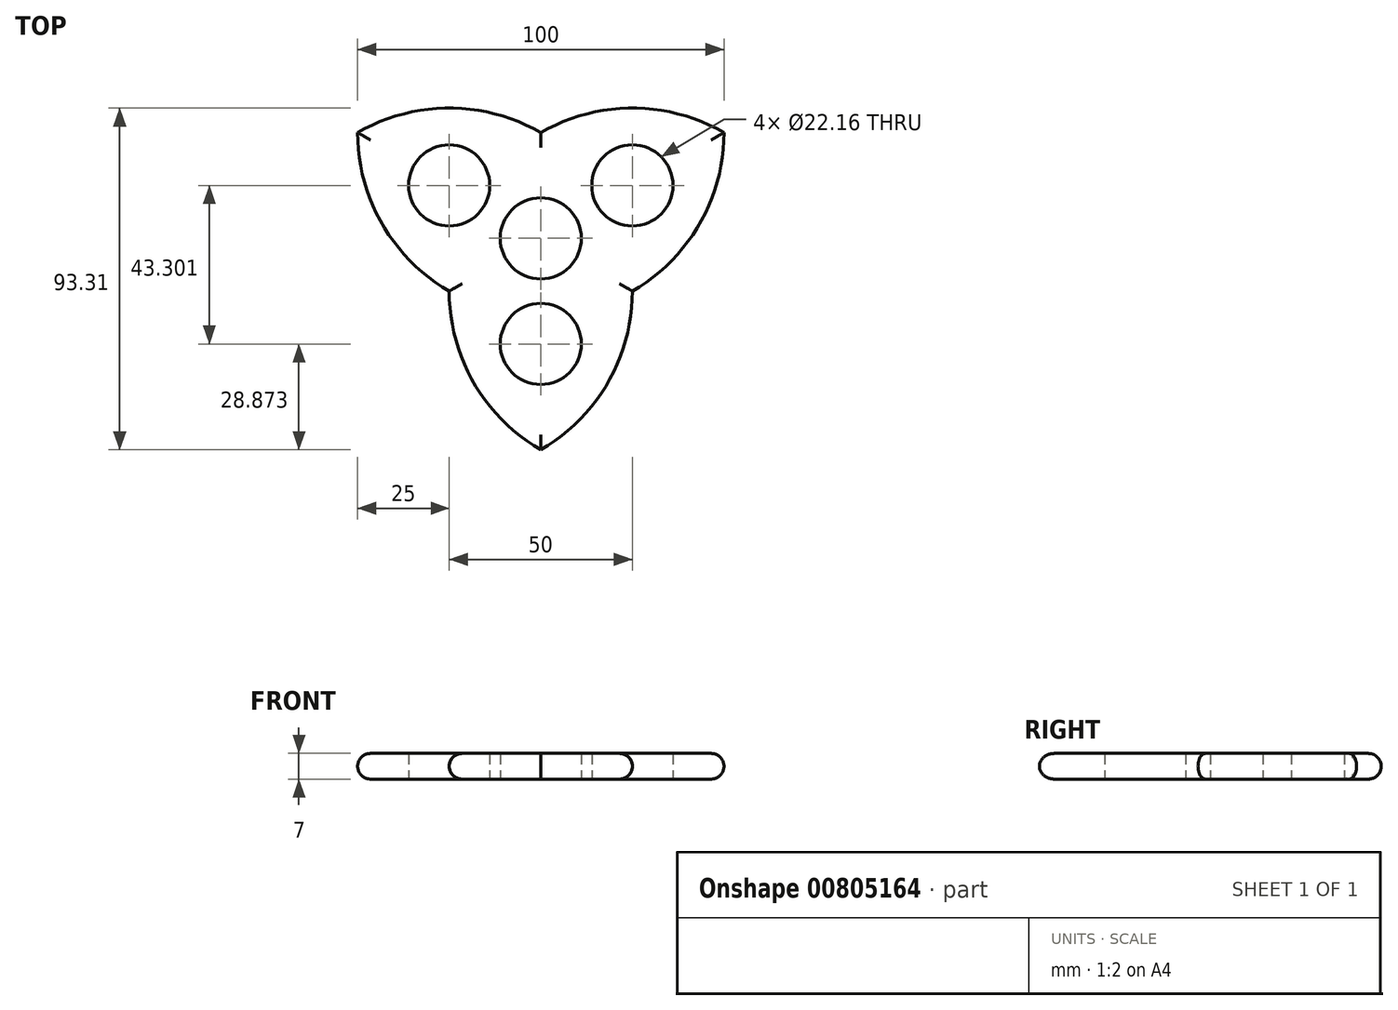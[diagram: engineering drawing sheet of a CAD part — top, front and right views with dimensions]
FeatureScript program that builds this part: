
annotation { "Feature Type Name" : "Feature", "Feature Type Description" : "" }
export const myFeature = defineFeature(function(context is Context, id is Id, definition is map)
    precondition{}
    {
        {
            var Q0;
            Q0=qCreatedBy(makeId("Top.planeOp"),FACE);
            var sketch = newSketch(context, id + "F0", { "sketchPlane" : qUnion([Q0])});
            skCircle(sketch, "E0.cCircle", {"center": v(0, 0) * mm, "radius": 14.43 * mm, "construction": true});
            skLineSegment(sketch, "E0.0", {"start": v(25, -14.43) * mm, "end": v(-25, -14.43) * mm, "construction": true});
            skLineSegment(sketch, "E0.1", {"start": v(-25, -14.43) * mm, "end": v(0, 28.87) * mm, "construction": true});
            skLineSegment(sketch, "E0.2", {"start": v(0, 28.87) * mm, "end": v(25, -14.43) * mm, "construction": true});
            skPoint(sketch, "E0.0.midPoint", {"position": v(0, -14.43) * mm});
            skArc(sketch, "E1", {"start": v(0, -57.74) * mm, "mid": v(18.3, -39.43) * mm, "end": v(25, -14.43) * mm});
            skArc(sketch, "E2", {"start": v(-50, 28.87) * mm, "mid": v(-43.3, 3.87) * mm, "end": v(-25, -14.43) * mm});
            skArc(sketch, "E3", {"start": v(50, 28.87) * mm, "mid": v(25, 35.57) * mm, "end": v(0, 28.87) * mm});
            skCircle(sketch, "E4", {"center": v(0, 0) * mm, "radius": 11.08 * mm});
            skArc(sketch, "E5.trimOffspring", {"start": v(0, 28.87) * mm, "mid": v(-25, 35.57) * mm, "end": v(-50, 28.87) * mm});
            skArc(sketch, "E6.trimOffspring", {"start": v(-25, -14.43) * mm, "mid": v(-18.3, -39.43) * mm, "end": v(0, -57.74) * mm});
            skArc(sketch, "E7.trimOffspring", {"start": v(25, -14.43) * mm, "mid": v(43.3, 3.87) * mm, "end": v(50, 28.87) * mm});
            skLineSegment(sketch, "E8", {"start": v(-25, -14.43) * mm, "end": v(-50, 28.87) * mm, "construction": true});
            skLineSegment(sketch, "E9", {"start": v(0, 28.87) * mm, "end": v(-50, 28.87) * mm, "construction": true});
            skLineSegment(sketch, "E10", {"start": v(-25, 28.87) * mm, "end": v(-25, -14.43) * mm, "construction": true});
            skLineSegment(sketch, "E11", {"start": v(0, 28.87) * mm, "end": v(-37.5, 7.22) * mm, "construction": true});
            skCircle(sketch, "E12", {"center": v(-25, 14.43) * mm, "radius": 11.08 * mm});
            skLineSegment(sketch, "E13.1.0", {"start": v(-25, -14.43) * mm, "end": v(0, -57.74) * mm, "construction": true});
            skLineSegment(sketch, "E13.1.1", {"start": v(25, -14.43) * mm, "end": v(0, -57.74) * mm, "construction": true});
            skCircle(sketch, "E13.1.2", {"center": v(0, -28.87) * mm, "radius": 11.08 * mm});
            skLineSegment(sketch, "E13.1.3", {"start": v(-25, -14.43) * mm, "end": v(12.5, -36.08) * mm, "construction": true});
            skLineSegment(sketch, "E13.1.4", {"start": v(-12.5, -36.08) * mm, "end": v(25, -14.43) * mm, "construction": true});
            skLineSegment(sketch, "E13.2.0", {"start": v(25, -14.43) * mm, "end": v(50, 28.87) * mm, "construction": true});
            skLineSegment(sketch, "E13.2.1", {"start": v(0, 28.87) * mm, "end": v(50, 28.87) * mm, "construction": true});
            skCircle(sketch, "E13.2.2", {"center": v(25, 14.43) * mm, "radius": 11.08 * mm});
            skLineSegment(sketch, "E13.2.3", {"start": v(25, -14.43) * mm, "end": v(25, 28.87) * mm, "construction": true});
            skLineSegment(sketch, "E13.2.4", {"start": v(37.5, 7.22) * mm, "end": v(0, 28.87) * mm, "construction": true});
            skSolve(sketch);
        }
        {
            var Q0;
            Q0=makeQuery(id+"F0.imprint","IMPRINT",FACE,{"disambiguationData":[TD([[makeQuery(id+"F0.imprint","IMPRINT",EDGE,{"derivedFrom":sQuery(id+"F0.wireOp",EDGE,"E1")}),1.0]])]});
            extrude(context, id + "F1", {"entities" : qUnion([Q0]), "depth" : 7 * mm, "offsetDistance" : 25 * mm});
        }
        {
            var Q0;
            Q0=makeQuery(id+"F1.opExtrude","CAP_EDGE",EDGE,{"disambiguationData":[OSD([sQuery(id+"F0.wireOp",EDGE,"E1")])],"isStart":false});
            var Q1;
            Q1=makeQuery(id+"F1.opExtrude","CAP_EDGE",EDGE,{"disambiguationData":[OSD([sQuery(id+"F0.wireOp",EDGE,"E7.trimOffspring")])],"isStart":false});
            var Q2;
            Q2=makeQuery(id+"F1.opExtrude","CAP_EDGE",EDGE,{"disambiguationData":[OSD([sQuery(id+"F0.wireOp",EDGE,"E3")])],"isStart":false});
            var Q3;
            Q3=makeQuery(id+"F1.opExtrude","CAP_EDGE",EDGE,{"disambiguationData":[OSD([sQuery(id+"F0.wireOp",EDGE,"E2")])],"isStart":false});
            var Q4;
            Q4=makeQuery(id+"F1.opExtrude","CAP_EDGE",EDGE,{"disambiguationData":[OSD([sQuery(id+"F0.wireOp",EDGE,"E6.trimOffspring")])],"isStart":false});
            var Q5;
            Q5=makeQuery(id+"F1.opExtrude","CAP_EDGE",EDGE,{"disambiguationData":[OSD([sQuery(id+"F0.wireOp",EDGE,"E3")])],"isStart":true});
            var Q6;
            Q6=makeQuery(id+"F1.opExtrude","CAP_EDGE",EDGE,{"disambiguationData":[OSD([sQuery(id+"F0.wireOp",EDGE,"E7.trimOffspring")])],"isStart":true});
            var Q7;
            Q7=makeQuery(id+"F1.opExtrude","CAP_EDGE",EDGE,{"disambiguationData":[OSD([sQuery(id+"F0.wireOp",EDGE,"E1")])],"isStart":true});
            var Q8;
            Q8=makeQuery(id+"F1.opExtrude","CAP_EDGE",EDGE,{"disambiguationData":[OSD([sQuery(id+"F0.wireOp",EDGE,"E6.trimOffspring")])],"isStart":true});
            var Q9;
            Q9=makeQuery(id+"F1.opExtrude","CAP_EDGE",EDGE,{"disambiguationData":[OSD([sQuery(id+"F0.wireOp",EDGE,"E2")])],"isStart":true});
            var Q10;
            Q10=makeQuery(id+"F1.opExtrude","CAP_EDGE",EDGE,{"disambiguationData":[OSD([sQuery(id+"F0.wireOp",EDGE,"E5.trimOffspring")])],"isStart":true});
            var Q11;
            Q11=makeQuery(id+"F1.opExtrude","CAP_EDGE",EDGE,{"disambiguationData":[OSD([sQuery(id+"F0.wireOp",EDGE,"E5.trimOffspring")])],"isStart":false});
            fillet(context, id + "F2", {"entities" : qUnion([Q0, Q1, Q2, Q3, Q4, Q5, Q6, Q7, Q8, Q9, Q10, Q11]), "radius" : 3.5 * mm, "tangentPropagation" : true, "allowEdgeOverflow" : false});
        }
    });
